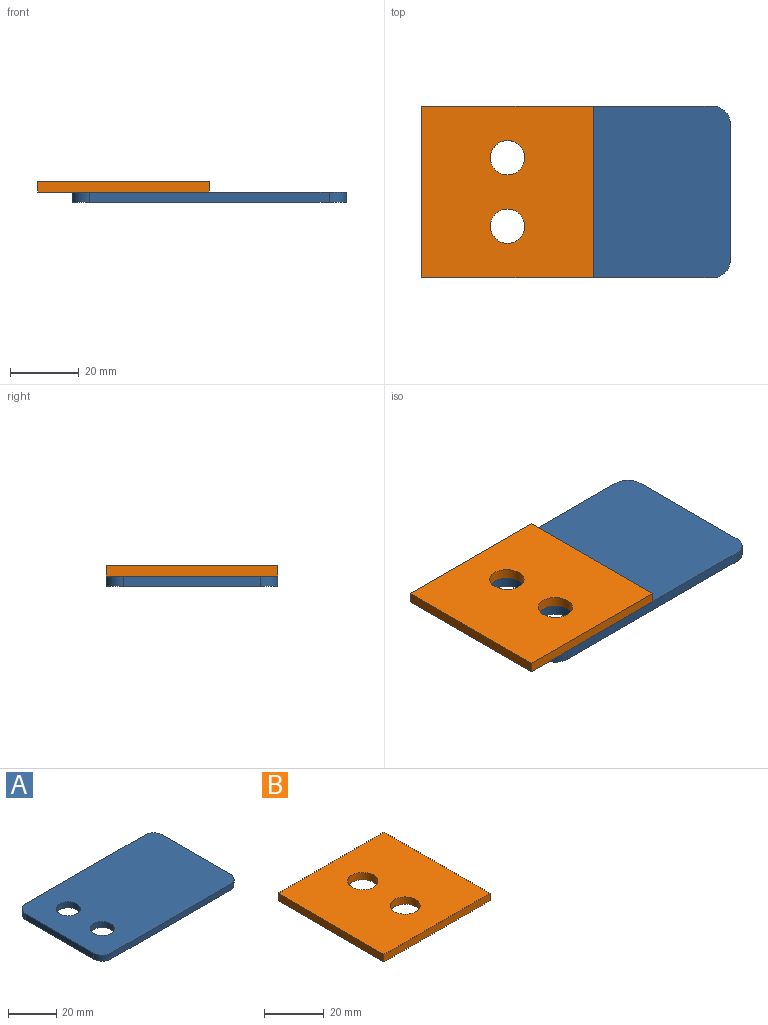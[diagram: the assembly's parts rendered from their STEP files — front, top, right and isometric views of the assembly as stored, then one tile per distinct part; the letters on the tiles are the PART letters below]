
ASSEMBLY  parts=2 mates=1
PART A: 12 faces, bbox 80x50x3 mm
  f0: plane 70x3mm, normal (0,-1,0), area 210mm2, adj f6,f7,f8,f11
  f1: plane 40x3mm, normal (1,0,0), area 120mm2, adj f6,f7,f8,f9
  f2: plane 70x3mm, normal (0,1,0), area 210mm2, adj f6,f7,f9,f10
  f3: cylinder r=5mm len=10mm, axis (0,0,-1), area 94.2mm2, adj f6,f7
  f4: cylinder r=5mm len=10mm, axis (0,0,-1), area 94.2mm2, adj f6,f7
  f5: plane 40x3mm, normal (-1,0,0), area 120mm2, adj f6,f7,f10,f11
  f6: plane 80x50mm, normal (0,0,1), area 3821.5mm2, adj f0,f1,f2,f3,f4,f5,f8,f9
  f7: plane 80x50mm, normal (0,0,-1), area 3821.5mm2, adj f0,f1,f2,f3,f4,f5,f8,f9
  f8: cylinder r=5mm len=5mm, axis (0,0,-1), area 23.6mm2, adj f0,f1,f6,f7
  f9: cylinder r=5mm len=5mm, axis (0,0,1), area 23.6mm2, adj f1,f2,f6,f7
  f10: cylinder r=5mm len=5mm, axis (0,0,-1), area 23.6mm2, adj f2,f5,f6,f7
  f11: cylinder r=5mm len=5mm, axis (0,0,1), area 23.6mm2, adj f0,f5,f6,f7
PART B: 8 faces, bbox 50x50x3 mm
  f0: plane 50x3mm, normal (1,0,0), area 150mm2, adj f1,f4,f6,f7
  f1: plane 50x3mm, normal (0,1,0), area 150mm2, adj f0,f2,f6,f7
  f2: plane 50x3mm, normal (-1,0,0), area 150mm2, adj f1,f4,f6,f7
  f3: cylinder r=5mm len=10mm, axis (0,0,-1), area 94.2mm2, adj f6,f7
  f4: plane 50x3mm, normal (0,-1,0), area 150mm2, adj f0,f2,f6,f7
  f5: cylinder r=5mm len=10mm, axis (0,0,-1), area 94.2mm2, adj f6,f7
  f6: plane 50x50mm, normal (0,0,1), area 2342.9mm2, adj f0,f1,f2,f3,f4,f5
  f7: plane 50x50mm, normal (0,0,-1), area 2342.9mm2, adj f0,f1,f2,f3,f4,f5
PLACE A t=(25,0,-3)mm
PLACE B at identity
MATE planar A.f4 <-> B.f5  axis (0,0,1) through (0,-10,0)mm
